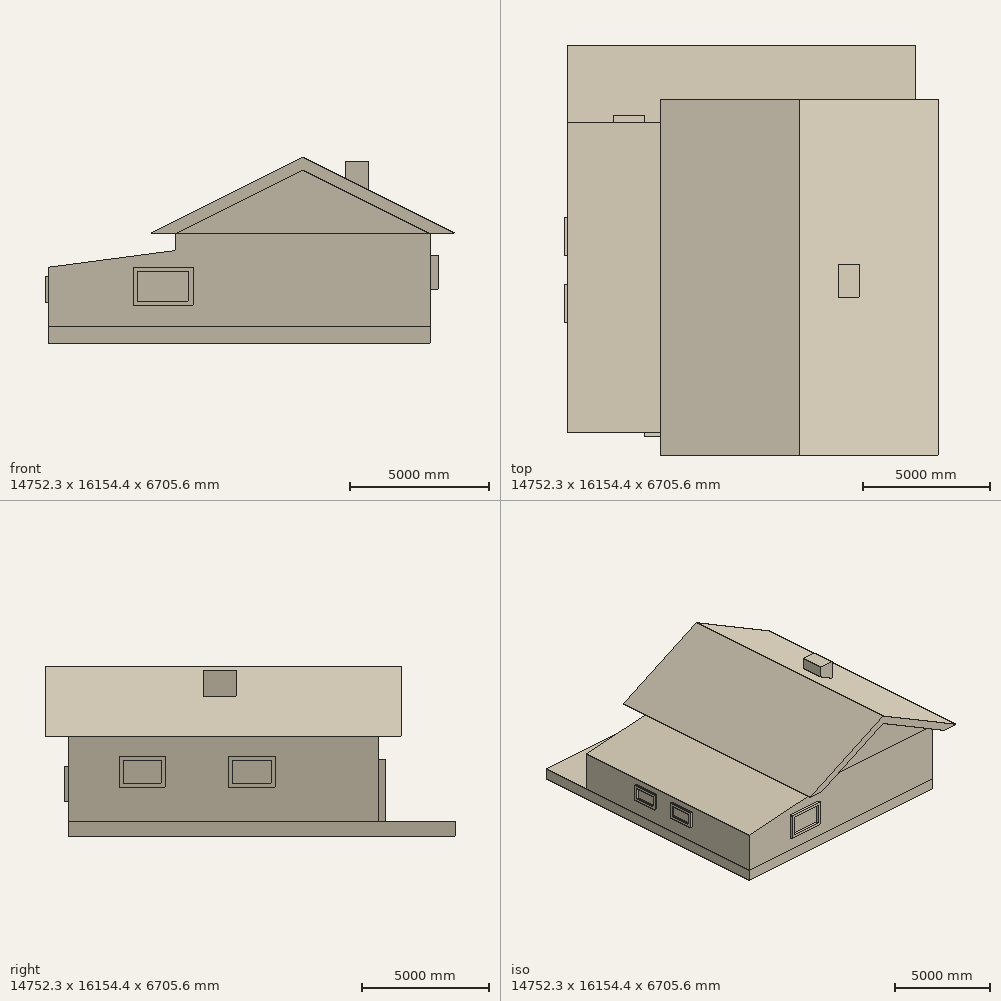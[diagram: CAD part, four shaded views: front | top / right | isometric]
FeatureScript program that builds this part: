
annotation { "Feature Type Name" : "Feature", "Feature Type Description" : "" }
export const myFeature = defineFeature(function(context is Context, id is Id, definition is map)
    precondition{}
    {
        {
            var Q0;
            Q0=qCreatedBy(makeId("Front.planeOp"),FACE);
            var sketch = newSketch(context, id + "F0", { "sketchPlane" : qUnion([Q0])});
            skLineSegment(sketch, "E0", {"start": v(0, 0) * mm, "end": v(-4572, 0) * mm});
            skLineSegment(sketch, "E1", {"start": v(0, 0) * mm, "end": v(4572, 0) * mm});
            skLineSegment(sketch, "E2", {"start": v(0, 0) * mm, "end": v(0, 2286) * mm});
            skLineSegment(sketch, "E3", {"start": v(4572, 0) * mm, "end": v(0, 2286) * mm});
            skLineSegment(sketch, "E4", {"start": v(-4572, 0) * mm, "end": v(0, 2286) * mm});
            skLineSegment(sketch, "E5", {"start": v(4572, 0) * mm, "end": v(5486.4, 0) * mm});
            skLineSegment(sketch, "E6", {"start": v(-4572, 0) * mm, "end": v(-5486.4, 0) * mm});
            skLineSegment(sketch, "E7", {"start": v(0, 2286) * mm, "end": v(0, 2743.2) * mm});
            skLineSegment(sketch, "E8", {"start": v(5486.4, 0) * mm, "end": v(0, 2743.2) * mm});
            skLineSegment(sketch, "E9", {"start": v(-5486.4, 0) * mm, "end": v(0, 2743.2) * mm});
            skLineSegment(sketch, "E10", {"start": v(4572, 0) * mm, "end": v(4572, -3352.8) * mm});
            skLineSegment(sketch, "E11", {"start": v(4572, -3352.8) * mm, "end": v(-4572, -3352.8) * mm});
            skLineSegment(sketch, "E12", {"start": v(-4572, -3352.8) * mm, "end": v(-4572, 0) * mm});
            skLineSegment(sketch, "E13", {"start": v(4572, -3352.8) * mm, "end": v(4572, -3962.4) * mm});
            skLineSegment(sketch, "E14", {"start": v(4572, -3962.4) * mm, "end": v(-4572, -3962.4) * mm});
            skLineSegment(sketch, "E15", {"start": v(-4572, -3962.4) * mm, "end": v(-4572, -3352.8) * mm});
            skLineSegment(sketch, "E16", {"start": v(3352.8, -3352.8) * mm, "end": v(3352.8, -1219.2) * mm});
            skLineSegment(sketch, "E17", {"start": v(3352.8, -1219.2) * mm, "end": v(2438.4, -1219.2) * mm});
            skLineSegment(sketch, "E18", {"start": v(2438.4, -1219.2) * mm, "end": v(2438.4, -3352.8) * mm});
            skLineSegment(sketch, "E19", {"start": v(2438.4, -3352.8) * mm, "end": v(3352.8, -3352.8) * mm});
            skLineSegment(sketch, "E20", {"start": v(-609.6, -1219.2) * mm, "end": v(-609.6, -2590.8) * mm});
            skLineSegment(sketch, "E21", {"start": v(-609.6, -2590.8) * mm, "end": v(-3352.8, -2590.8) * mm});
            skLineSegment(sketch, "E22", {"start": v(-3352.8, -2590.8) * mm, "end": v(-3352.8, -1219.2) * mm});
            skLineSegment(sketch, "E23", {"start": v(-3352.8, -1219.2) * mm, "end": v(-609.6, -1219.2) * mm});
            skLineSegment(sketch, "E24.0", {"start": v(-3505.2, -1066.8) * mm, "end": v(-457.2, -1066.8) * mm});
            skLineSegment(sketch, "E24.1", {"start": v(-3505.2, -2743.2) * mm, "end": v(-3505.2, -1066.8) * mm});
            skLineSegment(sketch, "E24.2", {"start": v(-457.2, -2743.2) * mm, "end": v(-3505.2, -2743.2) * mm});
            skLineSegment(sketch, "E24.3", {"start": v(-457.2, -1066.8) * mm, "end": v(-457.2, -2743.2) * mm});
            skLineSegment(sketch, "E25.0", {"start": v(2133.6, -914.4) * mm, "end": v(2133.6, -3352.8) * mm});
            skLineSegment(sketch, "E25.1", {"start": v(3657.6, -914.4) * mm, "end": v(2133.6, -914.4) * mm});
            skLineSegment(sketch, "E25.2", {"start": v(3657.6, -3352.8) * mm, "end": v(3657.6, -914.4) * mm});
            skLineSegment(sketch, "E26", {"start": v(-4572, -3962.4) * mm, "end": v(-9144, -3962.4) * mm});
            skLineSegment(sketch, "E27", {"start": v(-9144, -3962.4) * mm, "end": v(-9144, -3352.8) * mm});
            skLineSegment(sketch, "E28", {"start": v(-9144, -3352.8) * mm, "end": v(-4572, -3352.8) * mm});
            skLineSegment(sketch, "E29", {"start": v(-4572, -3352.8) * mm, "end": v(-4572, -609.6) * mm});
            skLineSegment(sketch, "E30", {"start": v(-4572, -609.6) * mm, "end": v(-4572, 0) * mm});
            skLineSegment(sketch, "E31", {"start": v(-9144, -3352.8) * mm, "end": v(-9144, -609.6) * mm});
            skLineSegment(sketch, "E32", {"start": v(-4572, 0) * mm, "end": v(-9144, -609.6) * mm});
            skLineSegment(sketch, "E33", {"start": v(-4572, -609.6) * mm, "end": v(-9144, -1212.83) * mm});
            skLineSegment(sketch, "E34.bottom", {"start": v(-6091, -1219.2) * mm, "end": v(-7310.2, -1219.2) * mm});
            skLineSegment(sketch, "E34.top", {"start": v(-6091, -2590.8) * mm, "end": v(-7310.2, -2590.8) * mm});
            skLineSegment(sketch, "E34.left", {"start": v(-6091, -1219.2) * mm, "end": v(-6091, -2590.8) * mm});
            skLineSegment(sketch, "E34.right", {"start": v(-7310.2, -1219.2) * mm, "end": v(-7310.2, -2590.8) * mm});
            skLineSegment(sketch, "E35.0", {"start": v(-6096, -1219.2) * mm, "end": v(-6096, -2590.8) * mm});
            skLineSegment(sketch, "E36.0", {"start": v(-6243.4, -1371.6) * mm, "end": v(-7157.8, -1371.6) * mm});
            skLineSegment(sketch, "E36.1", {"start": v(-6243.4, -1371.6) * mm, "end": v(-6243.4, -2438.4) * mm});
            skLineSegment(sketch, "E36.2", {"start": v(-6243.4, -2438.4) * mm, "end": v(-7157.8, -2438.4) * mm});
            skLineSegment(sketch, "E36.3", {"start": v(-7157.8, -1371.6) * mm, "end": v(-7157.8, -2438.4) * mm});
            skLineSegment(sketch, "E37", {"start": v(2358.86, 1563.77) * mm, "end": v(2358.86, 2584.78) * mm});
            skLineSegment(sketch, "E38", {"start": v(2358.86, 2584.78) * mm, "end": v(1524.36, 2584.78) * mm});
            skLineSegment(sketch, "E39", {"start": v(1524.36, 2584.78) * mm, "end": v(1524.36, 1981.02) * mm});
            skLineSegment(sketch, "E40", {"start": v(1524.36, 1981.02) * mm, "end": v(2358.86, 1563.77) * mm});
            skSolve(sketch);
        }
        {
            var Q0;
            Q0=makeQuery(id+"F0.imprint","IMPRINT",FACE,{"disambiguationData":[TD([[makeQuery(id+"F0.imprint","IMPRINT",EDGE,{"derivedFrom":sQuery(id+"F0.wireOp",EDGE,"E3")}),-1.0]])]});
            var Q1;
            Q1=makeQuery(id+"F0.imprint","IMPRINT",FACE,{"disambiguationData":[TD([[makeQuery(id+"F0.imprint","IMPRINT",EDGE,{"derivedFrom":sQuery(id+"F0.wireOp",EDGE,"E4")}),1.0]])]});
            var Q2;
            Q2=makeQuery(id+"F0.imprint","IMPRINT",FACE,{"disambiguationData":[TD([[makeQuery(id+"F0.imprint","IMPRINT",EDGE,{"derivedFrom":sQuery(id+"F0.wireOp",EDGE,"E30")}),1.0]])]});
            extrude(context, id + "F1", {"entities" : qUnion([Q0, Q1, Q2]), "depth" : 13106.4 * mm, "offsetDistance" : 30.48 * mm, "hasSecondDirection" : true, "secondDirectionOppositeDirection" : true, "secondDirectionDepth" : 914.4 * mm});
        }
        {
            var Q0;
            Q0=makeQuery(id+"F0.imprint","IMPRINT",FACE,{"disambiguationData":[TD([[makeQuery(id+"F0.imprint","IMPRINT",EDGE,{"derivedFrom":sQuery(id+"F0.wireOp",EDGE,"E1")}),1.0]])]});
            var Q1;
            Q1=makeQuery(id+"F0.imprint","IMPRINT",FACE,{"disambiguationData":[TD([[makeQuery(id+"F0.imprint","IMPRINT",EDGE,{"derivedFrom":sQuery(id+"F0.wireOp",EDGE,"E0")}),-1.0]])]});
            extrude(context, id + "F2", {"entities" : qUnion([Q0, Q1]), "operationType" : NewBodyOperationType.ADD, "depth" : 12344.4 * mm, "offsetDistance" : 30.48 * mm, "hasSecondDirection" : true, "secondDirectionOppositeDirection" : true, "secondDirectionDepth" : 152.4 * mm});
        }
        {
            var Q0;
            {var subQ5=sQuery(id+"F0.wireOp",EDGE,"E13");Q0=makeQuery(id+"F0.imprint","IMPRINT",FACE,{"disambiguationData":[TD([[makeQuery(id+"F0.imprint","IMPRINT",EDGE,{"derivedFrom":subQ5}),-1.0]])]});}
            var Q1;
            Q1=makeQuery(id+"F0.imprint","IMPRINT",FACE,{"disambiguationData":[TD([[makeQuery(id+"F0.imprint","IMPRINT",EDGE,{"derivedFrom":sQuery(id+"F0.wireOp",EDGE,"E15")}),1.0]])]});
            extrude(context, id + "F3", {"entities" : qUnion([Q0, Q1]), "depth" : 12192 * mm, "offsetDistance" : 30.48 * mm, "hasSecondDirection" : true, "secondDirectionOppositeDirection" : true, "secondDirectionDepth" : 3048 * mm});
        }
        {
            var Q0;
            Q0=makeQuery(id+"F0.imprint","IMPRINT",FACE,{"disambiguationData":[TD([[makeQuery(id+"F0.imprint","IMPRINT",EDGE,{"derivedFrom":sQuery(id+"F0.wireOp",EDGE,"E0")}),1.0]])]});
            var Q1;
            {var subQ1=sQuery(id+"F0.wireOp",EDGE,"E16");Q1=makeQuery(id+"F0.imprint","IMPRINT",FACE,{"disambiguationData":[TD([[makeQuery(id+"F0.imprint","IMPRINT",EDGE,{"derivedFrom":subQ1}),-1.0]])]});}
            var Q2;
            Q2=makeQuery(id+"F0.imprint","IMPRINT",FACE,{"disambiguationData":[TD([[makeQuery(id+"F0.imprint","IMPRINT",EDGE,{"derivedFrom":sQuery(id+"F0.wireOp",EDGE,"E16")}),1.0]])]});
            var Q3;
            Q3=makeQuery(id+"F0.imprint","IMPRINT",FACE,{"disambiguationData":[TD([[makeQuery(id+"F0.imprint","IMPRINT",EDGE,{"derivedFrom":sQuery(id+"F0.wireOp",EDGE,"E20")}),1.0]])]});
            var Q4;
            Q4=makeQuery(id+"F0.imprint","IMPRINT",FACE,{"disambiguationData":[TD([[makeQuery(id+"F0.imprint","IMPRINT",EDGE,{"derivedFrom":sQuery(id+"F0.wireOp",EDGE,"E20")}),-1.0]])]});
            var Q5;
            {var subQ1=sQuery(id+"F0.wireOp",EDGE,"E28");Q5=makeQuery(id+"F0.imprint","IMPRINT",FACE,{"disambiguationData":[TD([[makeQuery(id+"F0.imprint","IMPRINT",EDGE,{"derivedFrom":subQ1}),1.0]])]});}
            var Q6;
            {var subQ0=sQuery(id+"F0.wireOp",EDGE,"E34.right");Q6=makeQuery(id+"F0.imprint","IMPRINT",FACE,{"disambiguationData":[TD([[makeQuery(id+"F0.imprint","IMPRINT",EDGE,{"derivedFrom":subQ0}),1.0]])]});}
            var Q7;
            Q7=makeQuery(id+"F0.imprint","IMPRINT",FACE,{"disambiguationData":[TD([[makeQuery(id+"F0.imprint","IMPRINT",EDGE,{"derivedFrom":sQuery(id+"F0.wireOp",EDGE,"E36.0")}),1.0]])]});
            extrude(context, id + "F4", {"entities" : qUnion([Q0, Q1, Q2, Q3, Q4, Q5, Q6, Q7]), "depth" : 12192 * mm, "offsetDistance" : 30.48 * mm, "hasSecondDirection" : true, "secondDirectionOppositeDirection" : true, "secondDirectionDepth" : 30.48 * mm});
        }
        {
            var Q0;
            {var subQ0=sQuery(id+"F0.wireOp",EDGE,"E34.right");Q0=makeQuery(id+"F0.imprint","IMPRINT",FACE,{"disambiguationData":[TD([[makeQuery(id+"F0.imprint","IMPRINT",EDGE,{"derivedFrom":subQ0}),1.0]])]});}
            var Q1;
            Q1=makeQuery(id+"F0.imprint","IMPRINT",FACE,{"disambiguationData":[TD([[makeQuery(id+"F0.imprint","IMPRINT",EDGE,{"derivedFrom":sQuery(id+"F0.wireOp",EDGE,"E20")}),1.0]])]});
            var Q2;
            {var subQ1=sQuery(id+"F0.wireOp",EDGE,"E16");Q2=makeQuery(id+"F0.imprint","IMPRINT",FACE,{"disambiguationData":[TD([[makeQuery(id+"F0.imprint","IMPRINT",EDGE,{"derivedFrom":subQ1}),-1.0]])]});}
            extrude(context, id + "F5", {"entities" : qUnion([Q0, Q1, Q2]), "depth" : 30.48 * mm, "offsetDistance" : 30.48 * mm, "hasSecondDirection" : true, "secondDirectionOppositeDirection" : true, "secondDirectionDepth" : 304.8 * mm});
        }
        {
            var Q0;
            Q0=makeQuery(id+"F0.imprint","IMPRINT",FACE,{"disambiguationData":[TD([[makeQuery(id+"F0.imprint","IMPRINT",EDGE,{"derivedFrom":sQuery(id+"F0.wireOp",EDGE,"E16")}),1.0]])]});
            var Q1;
            Q1=makeQuery(id+"F0.imprint","IMPRINT",FACE,{"disambiguationData":[TD([[makeQuery(id+"F0.imprint","IMPRINT",EDGE,{"derivedFrom":sQuery(id+"F0.wireOp",EDGE,"E20")}),-1.0]])]});
            var Q2;
            Q2=makeQuery(id+"F0.imprint","IMPRINT",FACE,{"disambiguationData":[TD([[makeQuery(id+"F0.imprint","IMPRINT",EDGE,{"derivedFrom":sQuery(id+"F0.wireOp",EDGE,"E36.0")}),1.0]])]});
            extrude(context, id + "F6", {"entities" : qUnion([Q0, Q1, Q2]), "depth" : 30.48 * mm, "offsetDistance" : 30.48 * mm, "hasSecondDirection" : true, "secondDirectionOppositeDirection" : true, "secondDirectionDepth" : 152.4 * mm});
        }
        {
            var Q0;
            Q0=makeQuery(id+"F0.imprint","IMPRINT",FACE,{"disambiguationData":[TD([[makeQuery(id+"F0.imprint","IMPRINT",EDGE,{"derivedFrom":sQuery(id+"F0.wireOp",EDGE,"E37")}),1.0]])]});
            extrude(context, id + "F7", {"entities" : qUnion([Q0]), "operationType" : NewBodyOperationType.ADD, "depth" : 6891.53 * mm, "offsetDistance" : 30.48 * mm, "hasSecondDirection" : true, "secondDirectionOppositeDirection" : false, "secondDirectionDepth" : 5586.98 * mm});
        }
        {
            var Q0;
            Q0=makeQuery(id+"F4.opExtrude","SWEPT_FACE",FACE,{"disambiguationData":[OSD([sQuery(id+"F0.wireOp",EDGE,"E10")])]});
            var sketch = newSketch(context, id + "F8", { "sketchPlane" : qUnion([Q0])});
            skLineSegment(sketch, "E41", {"start": v(-10044.03, -955.7) * mm, "end": v(-10044.03, -1870.1) * mm});
            skLineSegment(sketch, "E42", {"start": v(-10044.03, -1870.1) * mm, "end": v(-8520.03, -1870.1) * mm});
            skLineSegment(sketch, "E43", {"start": v(-8520.03, -1870.1) * mm, "end": v(-8520.03, -955.7) * mm});
            skLineSegment(sketch, "E44", {"start": v(-8520.03, -955.7) * mm, "end": v(-10044.03, -955.7) * mm});
            skLineSegment(sketch, "E45", {"start": v(-5727.46, -955.7) * mm, "end": v(-5727.46, -1870.1) * mm});
            skLineSegment(sketch, "E46", {"start": v(-5727.46, -1870.1) * mm, "end": v(-4203.46, -1870.1) * mm});
            skLineSegment(sketch, "E47", {"start": v(-4203.46, -1870.1) * mm, "end": v(-4203.46, -955.7) * mm});
            skLineSegment(sketch, "E48", {"start": v(-5727.46, -955.7) * mm, "end": v(-4203.46, -955.7) * mm});
            skLineSegment(sketch, "E49.0", {"start": v(-8367.63, -803.3) * mm, "end": v(-10196.43, -803.3) * mm});
            skLineSegment(sketch, "E49.1", {"start": v(-8367.63, -2022.5) * mm, "end": v(-8367.63, -803.3) * mm});
            skLineSegment(sketch, "E49.2", {"start": v(-10196.43, -2022.5) * mm, "end": v(-8367.63, -2022.5) * mm});
            skLineSegment(sketch, "E49.3", {"start": v(-10196.43, -803.3) * mm, "end": v(-10196.43, -2022.5) * mm});
            skLineSegment(sketch, "E50.0", {"start": v(-5732.46, -925.23) * mm, "end": v(-5732.46, -1839.63) * mm});
            skLineSegment(sketch, "E51.0", {"start": v(-5879.86, -803.3) * mm, "end": v(-4051.06, -803.3) * mm});
            skLineSegment(sketch, "E51.1", {"start": v(-5879.86, -803.3) * mm, "end": v(-5879.86, -2022.5) * mm});
            skLineSegment(sketch, "E51.2", {"start": v(-5879.86, -2022.5) * mm, "end": v(-4051.06, -2022.5) * mm});
            skLineSegment(sketch, "E51.3", {"start": v(-4051.06, -2022.5) * mm, "end": v(-4051.06, -803.3) * mm});
            skSolve(sketch);
        }
        {
            var Q0;
            Q0=makeQuery(id+"F8.imprint","IMPRINT",FACE,{"disambiguationData":[TD([[makeQuery(id+"F8.imprint","IMPRINT",EDGE,{"derivedFrom":sQuery(id+"F8.wireOp",EDGE,"E41")}),-1.0]])]});
            var Q1;
            Q1=makeQuery(id+"F8.imprint","IMPRINT",FACE,{"disambiguationData":[TD([[makeQuery(id+"F8.imprint","IMPRINT",EDGE,{"derivedFrom":sQuery(id+"F8.wireOp",EDGE,"E45")}),-1.0]])]});
            extrude(context, id + "F9", {"entities" : qUnion([Q0, Q1]), "operationType" : NewBodyOperationType.ADD, "depth" : 304.8 * mm, "offsetDistance" : 30.48 * mm, "hasSecondDirection" : true, "secondDirectionOppositeDirection" : true, "secondDirectionDepth" : 1524 * mm});
        }
        {
            var Q0;
            Q0=makeQuery(id+"F4.opExtrude","SWEPT_FACE",FACE,{"disambiguationData":[OSD([sQuery(id+"F0.wireOp",EDGE,"E31")])]});
            var sketch = newSketch(context, id + "F10", { "sketchPlane" : qUnion([Q0])});
            skLineSegment(sketch, "E52", {"start": v(6359.37, -2465.95) * mm, "end": v(7883.37, -2465.95) * mm});
            skLineSegment(sketch, "E53", {"start": v(7883.37, -2465.95) * mm, "end": v(7883.37, -1551.55) * mm});
            skLineSegment(sketch, "E54", {"start": v(6359.37, -2465.95) * mm, "end": v(6359.37, -1551.55) * mm});
            skLineSegment(sketch, "E55", {"start": v(6359.37, -1551.55) * mm, "end": v(7883.37, -1551.55) * mm});
            skLineSegment(sketch, "E56.0", {"start": v(6511.77, -1703.95) * mm, "end": v(7730.97, -1703.95) * mm});
            skLineSegment(sketch, "E56.1", {"start": v(6511.77, -2313.55) * mm, "end": v(6511.77, -1703.95) * mm});
            skLineSegment(sketch, "E56.2", {"start": v(6511.77, -2313.55) * mm, "end": v(7730.97, -2313.55) * mm});
            skLineSegment(sketch, "E56.3", {"start": v(7730.97, -2313.55) * mm, "end": v(7730.97, -1703.95) * mm});
            skLineSegment(sketch, "E57", {"start": v(5234.54, -2465.95) * mm, "end": v(3710.54, -2465.95) * mm});
            skLineSegment(sketch, "E58", {"start": v(3710.54, -2465.95) * mm, "end": v(3710.54, -1551.55) * mm});
            skLineSegment(sketch, "E59", {"start": v(3710.54, -1551.55) * mm, "end": v(5234.54, -1551.55) * mm});
            skLineSegment(sketch, "E60", {"start": v(5234.54, -1551.55) * mm, "end": v(5234.54, -2465.95) * mm});
            skLineSegment(sketch, "E61.0", {"start": v(3862.94, -1703.95) * mm, "end": v(5082.14, -1703.95) * mm});
            skLineSegment(sketch, "E61.1", {"start": v(3862.94, -2313.55) * mm, "end": v(3862.94, -1703.95) * mm});
            skLineSegment(sketch, "E61.2", {"start": v(5082.14, -2313.55) * mm, "end": v(3862.94, -2313.55) * mm});
            skLineSegment(sketch, "E61.3", {"start": v(5082.14, -1703.95) * mm, "end": v(5082.14, -2313.55) * mm});
            skSolve(sketch);
        }
        {
            var Q0;
            Q0=makeQuery(id+"F10.imprint","IMPRINT",FACE,{"disambiguationData":[TD([[makeQuery(id+"F10.imprint","IMPRINT",EDGE,{"derivedFrom":sQuery(id+"F10.wireOp",EDGE,"E52")}),1.0]])]});
            var Q1;
            Q1=makeQuery(id+"F10.imprint","IMPRINT",FACE,{"disambiguationData":[TD([[makeQuery(id+"F10.imprint","IMPRINT",EDGE,{"derivedFrom":sQuery(id+"F10.wireOp",EDGE,"E57")}),-1.0]])]});
            extrude(context, id + "F11", {"entities" : qUnion([Q0, Q1]), "operationType" : NewBodyOperationType.ADD, "depth" : 121.92 * mm, "offsetDistance" : 30.48 * mm, "hasSecondDirection" : true, "secondDirectionOppositeDirection" : true, "secondDirectionDepth" : 579.12 * mm});
        }
        {
            var Q0;
            Q0=makeQuery(id+"F4.opExtrude","CAP_FACE",FACE,{"disambiguationData":[OSD([sQuery(id+"F0.wireOp",EDGE,"E0"),sQuery(id+"F0.wireOp",EDGE,"E1"),sQuery(id+"F0.wireOp",EDGE,"E10"),sQuery(id+"F0.wireOp",EDGE,"E11"),sQuery(id+"F0.wireOp",EDGE,"E19"),sQuery(id+"F0.wireOp",EDGE,"E28"),sQuery(id+"F0.wireOp",EDGE,"E30"),sQuery(id+"F0.wireOp",EDGE,"E31"),sQuery(id+"F0.wireOp",EDGE,"E33"),sQuery(id+"F0.wireOp",EDGE,"E34.bottom"),sQuery(id+"F0.wireOp",EDGE,"E34.top"),sQuery(id+"F0.wireOp",EDGE,"E34.left"),sQuery(id+"F0.wireOp",EDGE,"E35.0")])],"isStart":false});
            var sketch = newSketch(context, id + "F12", { "sketchPlane" : qUnion([Q0])});
            skLineSegment(sketch, "E62", {"start": v(-6091, -1219.2) * mm, "end": v(-6091, -2590.8) * mm});
            skLineSegment(sketch, "E63", {"start": v(-6091, -2590.8) * mm, "end": v(-3957.4, -2590.8) * mm});
            skLineSegment(sketch, "E64", {"start": v(-3957.4, -2590.8) * mm, "end": v(-3957.4, -1219.2) * mm});
            skLineSegment(sketch, "E65", {"start": v(-3957.4, -1219.2) * mm, "end": v(-6091, -1219.2) * mm});
            skLineSegment(sketch, "E66.0", {"start": v(-4109.8, -1371.6) * mm, "end": v(-5938.6, -1371.6) * mm});
            skLineSegment(sketch, "E66.1", {"start": v(-4109.8, -2438.4) * mm, "end": v(-4109.8, -1371.6) * mm});
            skLineSegment(sketch, "E66.2", {"start": v(-5938.6, -2438.4) * mm, "end": v(-4109.8, -2438.4) * mm});
            skLineSegment(sketch, "E66.3", {"start": v(-5938.6, -1371.6) * mm, "end": v(-5938.6, -2438.4) * mm});
            skSolve(sketch);
        }
        {
            var Q0;
            Q0=makeQuery(id+"F12.imprint","IMPRINT",FACE,{"disambiguationData":[TD([[makeQuery(id+"F12.imprint","IMPRINT",EDGE,{"derivedFrom":sQuery(id+"F12.wireOp",EDGE,"E62")}),1.0]])]});
            extrude(context, id + "F13", {"entities" : qUnion([Q0]), "operationType" : NewBodyOperationType.ADD, "depth" : 161.54 * mm, "offsetDistance" : 30.48 * mm});
        }
    });
